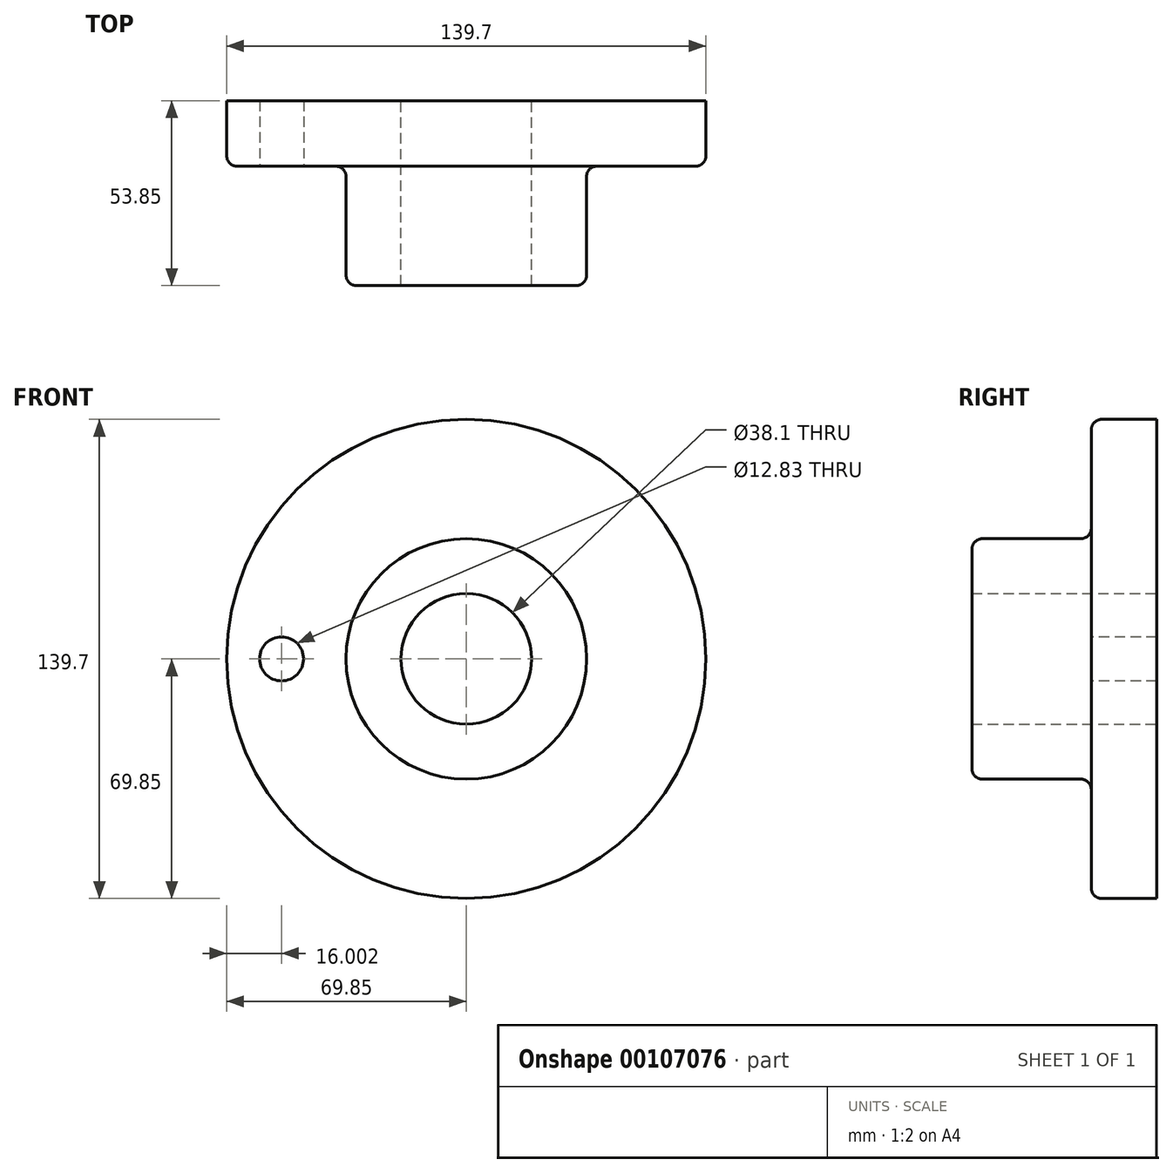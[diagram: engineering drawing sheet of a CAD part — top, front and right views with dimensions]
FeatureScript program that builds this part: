
annotation { "Feature Type Name" : "Feature", "Feature Type Description" : "" }
export const myFeature = defineFeature(function(context is Context, id is Id, definition is map)
    precondition{}
    {
        {
            var Q0;
            Q0=qCreatedBy(makeId("Right.planeOp"),FACE);
            var sketch = newSketch(context, id + "F0", { "sketchPlane" : qUnion([Q0])});
            skLineSegment(sketch, "E0", {"start": v(0, 19.05) * mm, "end": v(-53.85, 19.05) * mm});
            skLineSegment(sketch, "E1", {"start": v(-53.85, 19.05) * mm, "end": v(0, 19.05) * mm});
            skLineSegment(sketch, "E2", {"start": v(0, 69.85) * mm, "end": v(-19.05, 69.85) * mm});
            skLineSegment(sketch, "E3", {"start": v(-19.05, 69.85) * mm, "end": v(-19.05, 35.05) * mm});
            skLineSegment(sketch, "E4", {"start": v(-19.05, 35.05) * mm, "end": v(-53.85, 35.05) * mm});
            skLineSegment(sketch, "E5", {"start": v(-53.85, 35.05) * mm, "end": v(-53.85, 19.05) * mm});
            skLineSegment(sketch, "E6", {"start": v(0, 69.85) * mm, "end": v(0, 19.05) * mm});
            skLineSegment(sketch, "E7", {"start": v(0, 0) * mm, "end": v(-116.34, 0) * mm, "construction": true});
            skSolve(sketch);
        }
        {
            var Q0;
            Q0 = qSketchRegion(id + "F0", true);
            var Q1;
            Q1=sQuery(id+"F0.wireOp",EDGE,"E7");
            revolve(context, id + "F1", {"entities" : qUnion([Q0]), "axis" : qUnion([Q1]), "revolveType" : RevolveType.ONE_DIRECTION, "angle" : 360 * degree});
        }
        {
            var Q0;
            Q0=makeQuery(id+"F1.opRevolve","SWEPT_FACE",FACE,{"disambiguationData":[OSD([sQuery(id+"F0.wireOp",EDGE,"E3")])]});
            var sketch = newSketch(context, id + "F2", { "sketchPlane" : qUnion([Q0])});
            skCircle(sketch, "E8", {"center": v(0, 0) * mm, "radius": 53.85 * mm, "construction": true});
            skCircle(sketch, "E9", {"center": v(-53.85, 0) * mm, "radius": 6.42 * mm});
            skSolve(sketch);
        }
        {
            var Q0;
            Q0 = qSketchRegion(id + "F2", true);
            extrude(context, id + "F3", {"entities" : qUnion([Q0]), "operationType" : NewBodyOperationType.REMOVE, "endBound" : BoundingType.THROUGH_ALL, "oppositeDirection" : true, "depth" : 25.4 * mm});
        }
        {
            var Q0;
            Q0=makeQuery(id+"F1.opRevolve","SWEPT_EDGE",EDGE,{"disambiguationData":[OSD([sQuery(id+"F0.wireOp",EDGE,"E4"),sQuery(id+"F0.wireOp",EDGE,"E5")])]});
            var Q1;
            Q1=makeQuery(id+"F1.opRevolve","SWEPT_EDGE",EDGE,{"disambiguationData":[OSD([sQuery(id+"F0.wireOp",EDGE,"E3"),sQuery(id+"F0.wireOp",EDGE,"E4")])]});
            var Q2;
            Q2=makeQuery(id+"F1.opRevolve","SWEPT_EDGE",EDGE,{"disambiguationData":[OSD([sQuery(id+"F0.wireOp",EDGE,"E2"),sQuery(id+"F0.wireOp",EDGE,"E3")])]});
            fillet(context, id + "F4", {"entities" : qUnion([Q0, Q1, Q2]), "radius" : 3.05 * mm, "tangentPropagation" : true, "allowEdgeOverflow" : false});
        }
    });
